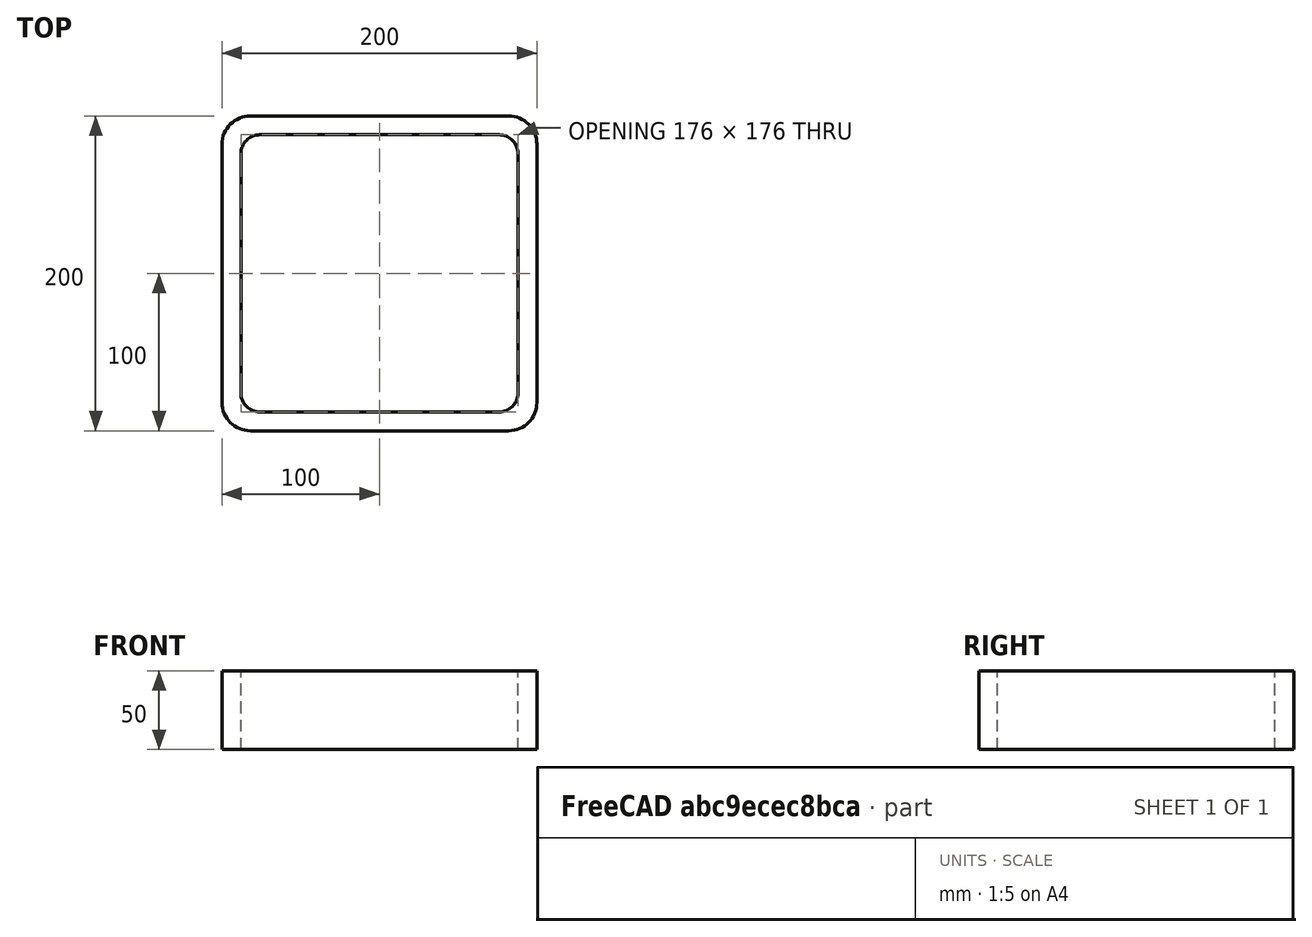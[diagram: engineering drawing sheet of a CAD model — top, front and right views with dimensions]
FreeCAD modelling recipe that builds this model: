
FCSTD DOCUMENT  (FreeCAD 0.15R4671 (Git))
Label: Square hollow section 200x200x12 EN10219 S235JRH
License: All rights reserved
LicenseURL: http://en.wikipedia.org/wiki/All_rights_reserved
objects: Sketcher::SketchObject×1, Part::Extrusion×1
note: 2 computed .brp shape members not serialized (recipe doc carries the construction recipe); baked Part::Feature solids carry a one-line shape summary decoded from their .brp

FEATURE [Sketcher::SketchObject] Sketch
  sketch-geometry (16):
    g0: LineSegment StartX=-76 StartY=88 StartZ=0 EndX=76 EndY=88 EndZ=0
    g1: LineSegment StartX=88 StartY=76 StartZ=0 EndX=88 EndY=-76 EndZ=0
    g2: LineSegment StartX=76 StartY=-88 StartZ=0 EndX=-76 EndY=-88 EndZ=0
    g3: LineSegment StartX=-88 StartY=-76 StartZ=0 EndX=-88 EndY=76 EndZ=0
    g4: LineSegment StartX=-82 StartY=100 StartZ=0 EndX=82 EndY=100 EndZ=0
    g5: LineSegment StartX=100 StartY=82 StartZ=0 EndX=100 EndY=-82 EndZ=0
    g6: LineSegment StartX=82 StartY=-100 StartZ=0 EndX=-82 EndY=-100 EndZ=0
    g7: LineSegment StartX=-100 StartY=-82 StartZ=0 EndX=-100 EndY=82 EndZ=0
    g8: ArcOfCircle CenterX=-76 CenterY=76 CenterZ=0 NormalX=0 NormalY=0 NormalZ=1 Radius=12 StartAngle=1.5708 EndAngle=3.14159
    g9: ArcOfCircle CenterX=76 CenterY=76 CenterZ=0 NormalX=0 NormalY=0 NormalZ=1 Radius=12 StartAngle=0 EndAngle=1.5708
    g10: ArcOfCircle CenterX=76 CenterY=-76 CenterZ=0 NormalX=0 NormalY=0 NormalZ=1 Radius=12 StartAngle=4.71239 EndAngle=6.28319
    g11: ArcOfCircle CenterX=-76 CenterY=-76 CenterZ=0 NormalX=0 NormalY=0 NormalZ=1 Radius=12 StartAngle=3.14159 EndAngle=4.71239
    g12: ArcOfCircle CenterX=82 CenterY=82 CenterZ=0 NormalX=0 NormalY=0 NormalZ=1 Radius=18 StartAngle=0 EndAngle=1.5708
    g13: ArcOfCircle CenterX=82 CenterY=-82 CenterZ=0 NormalX=0 NormalY=0 NormalZ=1 Radius=18 StartAngle=4.71239 EndAngle=6.28319
    g14: ArcOfCircle CenterX=-82 CenterY=-82 CenterZ=0 NormalX=0 NormalY=0 NormalZ=1 Radius=18 StartAngle=3.14159 EndAngle=4.71239
    g15: ArcOfCircle CenterX=-82 CenterY=82 CenterZ=0 NormalX=0 NormalY=0 NormalZ=1 Radius=18 StartAngle=1.5708 EndAngle=3.14159
  constraints (36):
    c: Horizontal(g2)
    c: Vertical(g3)
    c: Horizontal(g6)
    c: Vertical(g7)
    c: Tangent(g3,g8) = 1.5708
    c: Tangent(g0,g8) = 1.5708
    c: Tangent(g0,g9) = 1.5708
    c: Tangent(g1,g9) = 1.5708
    c: Tangent(g1,g10) = 1.5708
    c: Tangent(g2,g10) = 1.5708
    c: Tangent(g2,g11) = 1.5708
    c: Tangent(g3,g11) = 1.5708
    c: Tangent(g4,g12) = 1.5708
    c: Tangent(g5,g12) = 1.5708
    c: Tangent(g5,g13) = 1.5708
    c: Tangent(g6,g13) = 1.5708
    c: Tangent(g6,g14) = 1.5708
    c: Tangent(g7,g14) = 1.5708
    c: Tangent(g7,g15) = 1.5708
    c: Tangent(g4,g15) = 1.5708
    c: Equal(g9,g8)
    c: Equal(g9,g11)
    c: Equal(g9,g10)
    c: Equal(g12,g15)
    c: Equal(g12,g14)
    c: Equal(g12,g13)
    c: Symmetric(g4,g6,g-1)
    c: Symmetric(g7,g5,g-2)
    c: DistanceY(g4,g6) = -200
    c: DistanceX(g7,g5) = 200
    c: Symmetric(g3,g1,g-2)
    c: Symmetric(g0,g2,g-1)
    c: DistanceY(g0,g4) = 12
    c: DistanceX(g5,g1) = -12
    c: Radius(g9) = 12
    c: Radius(g12) = 18
FEATURE [Part::Extrusion] Extrude  label="Square hollow section 200x200x12 EN10219 S235JRH"
  Base = -> Sketch
  Dir = (0,0,50)
  Solid = true
